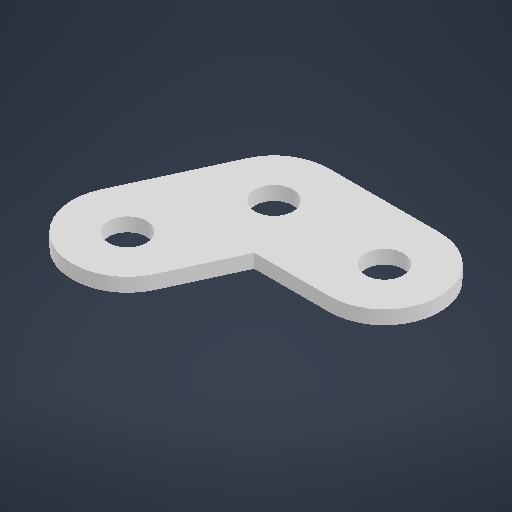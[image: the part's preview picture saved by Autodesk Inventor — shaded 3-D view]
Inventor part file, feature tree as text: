
AUTODESK INVENTOR PART (.ipt)
format: ipt  version: 2025.2 (Build 292293000, 293)  size: 195,072 bytes
history: native  units: in
note: dims shown in document units (in); Inventor stores cm internally (conversion verified against a paired STEP export)
features: extrude x1, sketch x1
ambient origin geometry x8: Origin, YZ Plane, XZ Plane, XY Plane, X Axis, Y Axis, Z Axis, Center Point
bodies: Solid1 (feature_tree)
feature tree (2):
  extrude  "Extrusion1"  Depth=0.5in
  sketch  "Sketch1"  dims[d0=0.5in d1=0.5in d2=0.5in d3=0.0625in d4=0.0in]
